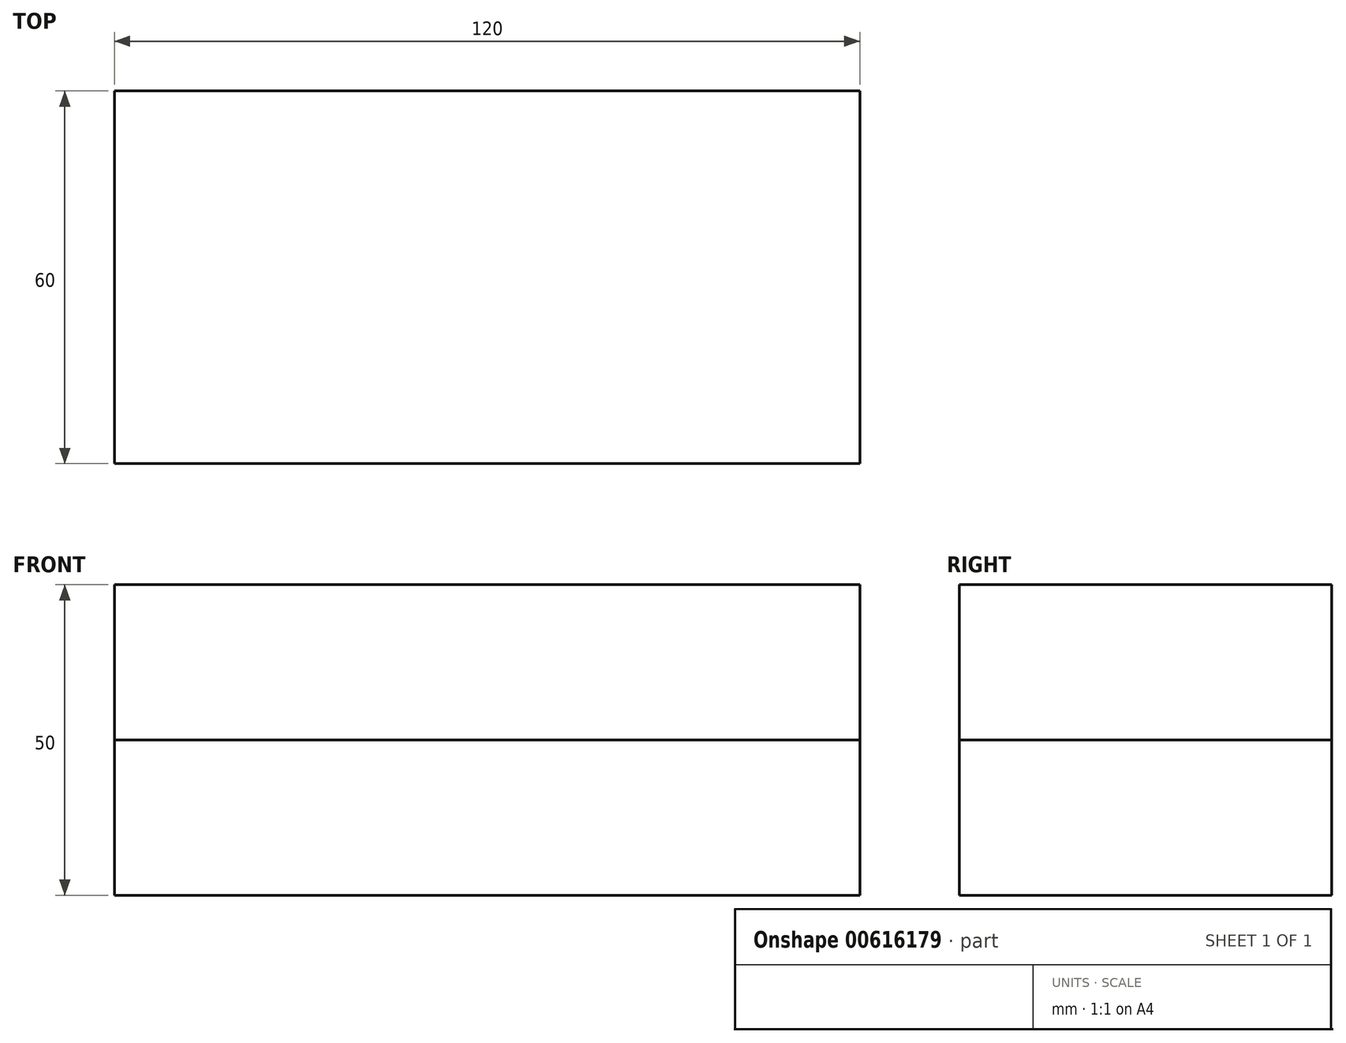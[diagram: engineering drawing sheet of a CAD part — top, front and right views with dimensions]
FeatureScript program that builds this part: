
annotation { "Feature Type Name" : "Feature", "Feature Type Description" : "" }
export const myFeature = defineFeature(function(context is Context, id is Id, definition is map)
    precondition{}
    {
        {
            var Q0;
            Q0=qCreatedBy(makeId("Top.planeOp"),FACE);
            var sketch = newSketch(context, id + "F0", { "sketchPlane" : qUnion([Q0])});
            skLineSegment(sketch, "E0.bottom", {"start": v(0, 0) * mm, "end": v(120, 0) * mm});
            skLineSegment(sketch, "E0.top", {"start": v(0, 60) * mm, "end": v(120, 60) * mm});
            skLineSegment(sketch, "E0.left", {"start": v(0, 0) * mm, "end": v(0, 60) * mm});
            skLineSegment(sketch, "E0.right", {"start": v(120, 0) * mm, "end": v(120, 60) * mm});
            skSolve(sketch);
        }
        {
            var Q0;
            Q0 = qSketchRegion(id + "F0", true);
            extrude(context, id + "F1", {"entities" : qUnion([Q0]), "depth" : 25 * mm, "offsetDistance" : 25 * mm});
        }
        {
            var Q0;
            Q0=qCreatedBy(makeId("Top.planeOp"),FACE);
            var sketch = newSketch(context, id + "F2", { "sketchPlane" : qUnion([Q0])});
            skLineSegment(sketch, "E1", {"start": v(0, 29.32) * mm, "end": v(119.7, 29.32) * mm, "construction": true});
            skLineSegment(sketch, "E2", {"start": v(25.8, 59.83) * mm, "end": v(25.8, 0) * mm, "construction": true});
            skLineSegment(sketch, "E3", {"start": v(55.72, 59.83) * mm, "end": v(55.72, 0) * mm, "construction": true});
            skLineSegment(sketch, "E4", {"start": v(88.6, 59.63) * mm, "end": v(88.6, 0) * mm, "construction": true});
            skCircle(sketch, "E5", {"center": v(25.8, 29.32) * mm, "radius": 12.92 * mm});
            skCircle(sketch, "E6", {"center": v(55.72, 29.32) * mm, "radius": 13.8 * mm});
            skCircle(sketch, "E7", {"center": v(88.6, 29.82) * mm, "radius": 14.38 * mm});
            skSolve(sketch);
        }
        {
            var Q0;
            Q0=makeQuery(id+"F1.opExtrude","CAP_FACE",FACE,{"disambiguationData":[OSD([sQuery(id+"F0.wireOp",EDGE,"E0.bottom"),sQuery(id+"F0.wireOp",EDGE,"E0.top"),sQuery(id+"F0.wireOp",EDGE,"E0.left"),sQuery(id+"F0.wireOp",EDGE,"E0.right")])],"isStart":false});
            extrude(context, id + "F3", {"entities" : qUnion([Q0]), "depth" : 25 * mm, "offsetDistance" : 25 * mm});
        }
        {
            var Q0;
            Q0=makeQuery(id+"F3.opExtrude","CAP_FACE",FACE,{"disambiguationData":[OSD([sQuery(id+"F0.wireOp",EDGE,"E0.bottom"),sQuery(id+"F0.wireOp",EDGE,"E0.top"),sQuery(id+"F0.wireOp",EDGE,"E0.left"),sQuery(id+"F0.wireOp",EDGE,"E0.right")])],"isStart":false});
            var Q1;
            Q1=sQuery(id+"F2.wireOp",EDGE,"E6");
            var Q2;
            Q2=sQuery(id+"F2.wireOp",EDGE,"E7");
            var Q3;
            Q3=sQuery(id+"F2.wireOp",EDGE,"E5");
            extrude(context, id + "F4", {"entities" : qUnion([Q0]), "bodyType" : ToolBodyType.SURFACE, "surfaceEntities" : qUnion([Q1, Q2, Q3]), "depth" : 25 * mm, "offsetDistance" : 25 * mm, "hasSecondDirection" : true, "secondDirectionOppositeDirection" : true, "secondDirectionDepth" : 25 * mm});
        }
    });
